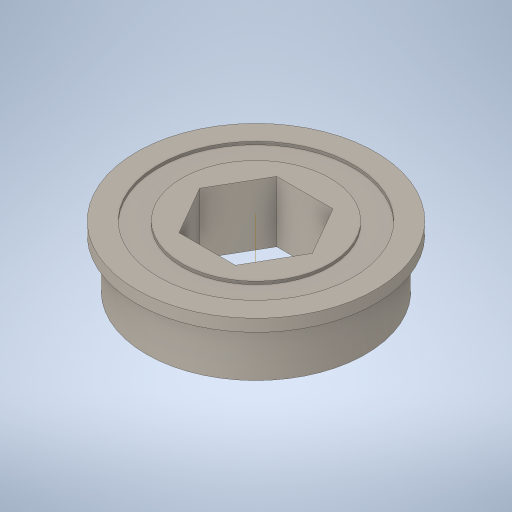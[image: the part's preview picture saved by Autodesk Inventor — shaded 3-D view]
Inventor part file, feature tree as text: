
AUTODESK INVENTOR PART (.ipt)
format: ipt  version: 2023.3 (Build 273359000, 359)  size: 292,864 bytes
history: native  units: in
note: dims shown in document units (in); Inventor stores cm internally (conversion verified against a paired STEP export)
features: revolve x1, sketch x1, other x1
ambient origin geometry x8: Origin, YZ Plane, XZ Plane, XY Plane, X Axis, Y Axis, Z Axis, Center Point
bodies: Solid1 (feature_tree)
feature tree (3):
  revolve  "Revolution1"  [1 undecoded]
  sketch  "Sketch1"  dims[d0=90.0deg]
  other  "Cut-Extrude1"
note: 1 required parameter value undecoded (feature->parameter linkage not recoverable at this tier; creation-order binding heuristic only, values carry confidence <= 0.55)
